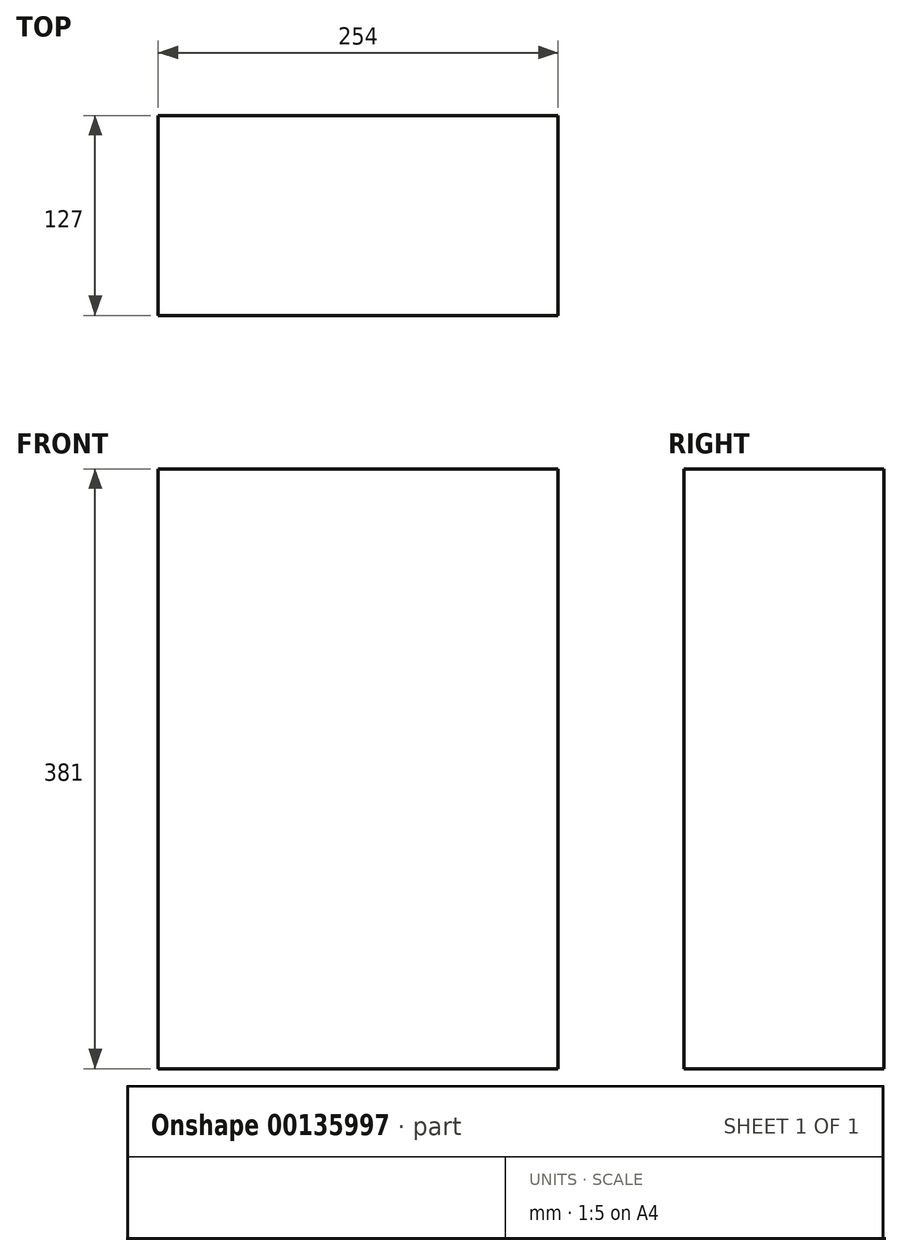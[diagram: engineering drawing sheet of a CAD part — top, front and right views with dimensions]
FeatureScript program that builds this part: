
annotation { "Feature Type Name" : "Feature", "Feature Type Description" : "" }
export const myFeature = defineFeature(function(context is Context, id is Id, definition is map)
    precondition{}
    {
        {
            var Q0;
            Q0=qCreatedBy(makeId("Front.planeOp"),FACE);
            var sketch = newSketch(context, id + "F0", { "sketchPlane" : qUnion([Q0])});
            skLineSegment(sketch, "E0.bottom", {"start": v(-127, 190.5) * mm, "end": v(127, 190.5) * mm});
            skLineSegment(sketch, "E0.top", {"start": v(-127, -190.5) * mm, "end": v(127, -190.5) * mm});
            skLineSegment(sketch, "E0.left", {"start": v(-127, 190.5) * mm, "end": v(-127, -190.5) * mm});
            skLineSegment(sketch, "E0.right", {"start": v(127, 190.5) * mm, "end": v(127, -190.5) * mm});
            skSolve(sketch);
        }
        {
            var Q0;
            Q0 = qSketchRegion(id + "F0", true);
            extrude(context, id + "F1", {"entities" : qUnion([Q0]), "depth" : 127 * mm});
        }
    });
